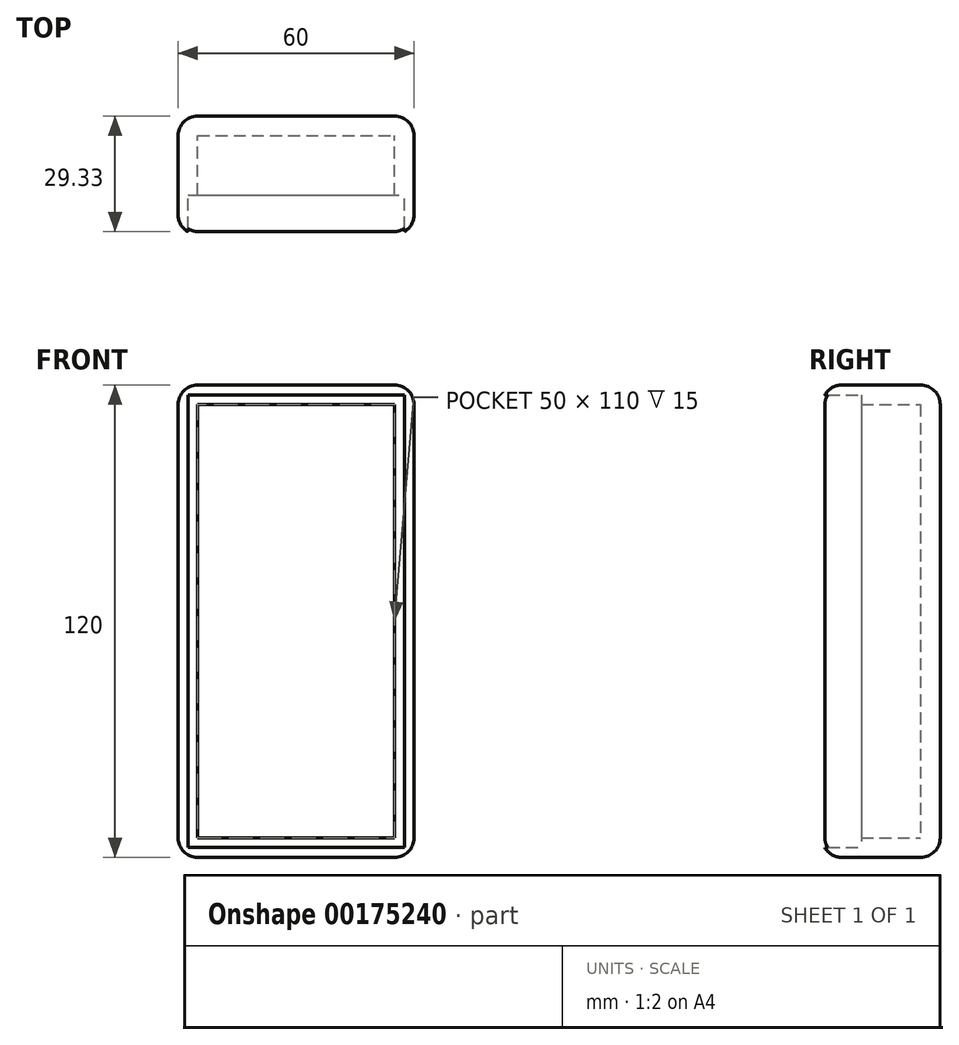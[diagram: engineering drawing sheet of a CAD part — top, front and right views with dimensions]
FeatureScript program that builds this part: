
annotation { "Feature Type Name" : "Feature", "Feature Type Description" : "" }
export const myFeature = defineFeature(function(context is Context, id is Id, definition is map)
    precondition{}
    {
        {
            var Q0;
            Q0=qCreatedBy(makeId("Front.planeOp"),FACE);
            var sketch = newSketch(context, id + "F0", { "sketchPlane" : qUnion([Q0])});
            skLineSegment(sketch, "E0.bottom", {"start": v(-21.77, 80.13) * mm, "end": v(33.23, 80.13) * mm});
            skLineSegment(sketch, "E0.top", {"start": v(-26.77, -39.87) * mm, "end": v(33.23, -39.87) * mm});
            skLineSegment(sketch, "E0.left", {"start": v(-26.77, 80.13) * mm, "end": v(-26.77, -39.87) * mm});
            skLineSegment(sketch, "E0.right", {"start": v(33.23, 80.13) * mm, "end": v(33.23, -39.87) * mm});
            skLineSegment(sketch, "E1.right", {"start": v(-21.77, 80.13) * mm, "end": v(-21.77, 80.13) * mm});
            skLineSegment(sketch, "E2.bottom", {"start": v(-21.77, 75.13) * mm, "end": v(28.23, 75.13) * mm});
            skLineSegment(sketch, "E2.top", {"start": v(-21.77, -34.87) * mm, "end": v(28.23, -34.87) * mm});
            skLineSegment(sketch, "E2.left", {"start": v(-21.77, 75.13) * mm, "end": v(-21.77, -34.87) * mm});
            skLineSegment(sketch, "E2.right", {"start": v(28.23, 75.13) * mm, "end": v(28.23, -34.87) * mm});
            skLineSegment(sketch, "E3", {"start": v(-21.77, 80.13) * mm, "end": v(-26.77, 80.13) * mm});
            skLineSegment(sketch, "E4", {"start": v(-26.77, 80.13) * mm, "end": v(-24.27, 80.13) * mm});
            skLineSegment(sketch, "E5.bottom", {"start": v(-24.27, 77.63) * mm, "end": v(30.73, 77.63) * mm});
            skLineSegment(sketch, "E5.top", {"start": v(-24.27, -37.37) * mm, "end": v(30.73, -37.37) * mm});
            skLineSegment(sketch, "E5.left", {"start": v(-24.27, 77.63) * mm, "end": v(-24.27, -37.37) * mm});
            skLineSegment(sketch, "E5.right", {"start": v(30.73, 77.63) * mm, "end": v(30.73, -37.37) * mm});
            skSolve(sketch);
        }
        {
            var Q0;
            Q0=makeQuery(id+"F0.imprint","IMPRINT",FACE,{"disambiguationData":[TD([[makeQuery(id+"F0.imprint","IMPRINT",EDGE,{"derivedFrom":sQuery(id+"F0.wireOp",EDGE,"E0.bottom")}),-1.0]])]});
            var Q1;
            Q1=makeQuery(id+"F0.imprint","IMPRINT",FACE,{"disambiguationData":[TD([[makeQuery(id+"F0.imprint","IMPRINT",EDGE,{"derivedFrom":sQuery(id+"F0.wireOp",EDGE,"E2.bottom")}),1.0]])]});
            extrude(context, id + "F1", {"entities" : qUnion([Q0, Q1]), "depth" : 20 * mm});
        }
        {
            var Q0;
            Q0=makeQuery(id+"F1.opExtrude","CAP_FACE",FACE,{"disambiguationData":[OSD([sQuery(id+"F0.wireOp",EDGE,"E0.bottom"),sQuery(id+"F0.wireOp",EDGE,"E0.top"),sQuery(id+"F0.wireOp",EDGE,"E0.left"),sQuery(id+"F0.wireOp",EDGE,"E0.right"),sQuery(id+"F0.wireOp",EDGE,"E2.bottom"),sQuery(id+"F0.wireOp",EDGE,"E2.top"),sQuery(id+"F0.wireOp",EDGE,"E2.left"),sQuery(id+"F0.wireOp",EDGE,"E2.right"),sQuery(id+"F0.wireOp",EDGE,"E3"),sQuery(id+"F0.wireOp",EDGE,"E4")])],"isStart":false});
            var sketch = newSketch(context, id + "F2", { "sketchPlane" : qUnion([Q0])});
            skLineSegment(sketch, "E6.left", {"start": v(-26.77, 80.13) * mm, "end": v(-26.77, 80.13) * mm});
            skLineSegment(sketch, "E6.right", {"start": v(-24.27, 80.13) * mm, "end": v(-24.27, 80.13) * mm});
            skLineSegment(sketch, "E7.bottom", {"start": v(-24.27, 77.63) * mm, "end": v(30.73, 77.63) * mm});
            skLineSegment(sketch, "E7.top", {"start": v(-24.27, -37.37) * mm, "end": v(30.73, -37.37) * mm});
            skLineSegment(sketch, "E7.left", {"start": v(-24.27, 77.63) * mm, "end": v(-24.27, -37.37) * mm});
            skLineSegment(sketch, "E7.right", {"start": v(30.73, 77.63) * mm, "end": v(30.73, -37.37) * mm});
            skPoint(sketch, "E8.end.orphan", {"position": v(-26.77, 77.63) * mm});
            skSolve(sketch);
        }
        {
            var Q0;
            Q0=makeQuery(id+"F2.imprint","IMPRINT",FACE,{"disambiguationData":[TD([[makeQuery(id+"F2.imprint","IMPRINT",EDGE,{"derivedFrom":sQuery(id+"F2.wireOp",EDGE,"E7.bottom")}),1.0]])]});
            extrude(context, id + "F3", {"entities" : qUnion([Q0]), "operationType" : NewBodyOperationType.ADD, "depth" : 10 * mm});
        }
        {
            var Q0;
            Q0=makeQuery(id+"F3.opExtrude","CAP_EDGE",EDGE,{"disambiguationData":[OSD([sQuery(id+"F0.wireOp",EDGE,"E0.top")])],"isStart":false});
            var Q1;
            Q1=makeQuery(id+"F3.opExtrude","CAP_EDGE",EDGE,{"disambiguationData":[OSD([sQuery(id+"F0.wireOp",EDGE,"E0.left")])],"isStart":false});
            var Q2;
            Q2=makeQuery(id+"F3.opExtrude","CAP_EDGE",EDGE,{"disambiguationData":[OSD([sQuery(id+"F0.wireOp",EDGE,"E0.bottom"),sQuery(id+"F0.wireOp",EDGE,"E3"),sQuery(id+"F0.wireOp",EDGE,"E4")])],"isStart":false});
            var Q3;
            Q3=makeQuery(id+"F3.opExtrude","CAP_EDGE",EDGE,{"disambiguationData":[OSD([sQuery(id+"F0.wireOp",EDGE,"E0.right")])],"isStart":false});
            fillet(context, id + "F4", {"entities" : qUnion([Q0, Q1, Q2, Q3]), "radius" : 5 * mm, "tangentPropagation" : true, "allowEdgeOverflow" : false});
        }
        {
            var Q0;
            Q0=makeQuery(id+"F1.opExtrude","CAP_FACE",FACE,{"disambiguationData":[OSD([sQuery(id+"F0.wireOp",EDGE,"E0.bottom"),sQuery(id+"F0.wireOp",EDGE,"E0.top"),sQuery(id+"F0.wireOp",EDGE,"E0.left"),sQuery(id+"F0.wireOp",EDGE,"E0.right"),sQuery(id+"F0.wireOp",EDGE,"E2.bottom"),sQuery(id+"F0.wireOp",EDGE,"E2.top"),sQuery(id+"F0.wireOp",EDGE,"E2.left"),sQuery(id+"F0.wireOp",EDGE,"E2.right"),sQuery(id+"F0.wireOp",EDGE,"E3"),sQuery(id+"F0.wireOp",EDGE,"E4")])],"isStart":true});
            var sketch = newSketch(context, id + "F5", { "sketchPlane" : qUnion([Q0])});
            skSolve(sketch);
        }
        {
            var Q0;
            Q0 = qSketchRegion(id + "F5", true);
            var Q1;
            Q1=makeQuery(id+"F5.imprint","IMPRINT",FACE,{"disambiguationData":[TD([[makeQuery(id+"F5.imprint","IMPRINT",EDGE,{"derivedFrom":makeQuery(id+"F1.opExtrude","CAP_EDGE",EDGE,{"disambiguationData":[OSD([sQuery(id+"F0.wireOp",EDGE,"E2.bottom")])],"isStart":true})}),1.0]])]});
            extrude(context, id + "F6", {"entities" : qUnion([Q0, Q1]), "operationType" : NewBodyOperationType.ADD, "oppositeDirection" : true, "depth" : 5 * mm});
        }
        {
            var Q0;
            {var subQ0=sQuery(id+"F0.wireOp",EDGE,"E0.right");var subQ1=sQuery(id+"F0.wireOp",EDGE,"E0.bottom");Q0=makeQuery(id+"F3.boolean.opBoolean","MERGE",EDGE,{"derivedFrom":[makeQuery(id+"F1.opExtrude","SWEPT_EDGE",EDGE,{"disambiguationData":[OSD([subQ1,subQ0])]}),makeQuery(id+"F3.opExtrude","SWEPT_EDGE",EDGE,{"disambiguationData":[OSD([subQ1,subQ0,sQuery(id+"F0.wireOp",EDGE,"E3"),sQuery(id+"F0.wireOp",EDGE,"E4")])]})]});}
            var Q1;
            Q1=makeQuery(id+"F1.opExtrude","CAP_EDGE",EDGE,{"disambiguationData":[OSD([sQuery(id+"F0.wireOp",EDGE,"E0.right")])],"isStart":true});
            var Q2;
            Q2=makeQuery(id+"F1.opExtrude","CAP_EDGE",EDGE,{"disambiguationData":[OSD([sQuery(id+"F0.wireOp",EDGE,"E0.bottom"),sQuery(id+"F0.wireOp",EDGE,"E3"),sQuery(id+"F0.wireOp",EDGE,"E4")])],"isStart":true});
            var Q3;
            Q3=makeQuery(id+"F1.opExtrude","CAP_EDGE",EDGE,{"disambiguationData":[OSD([sQuery(id+"F0.wireOp",EDGE,"E0.left")])],"isStart":true});
            var Q4;
            Q4=makeQuery(id+"F1.opExtrude","CAP_EDGE",EDGE,{"disambiguationData":[OSD([sQuery(id+"F0.wireOp",EDGE,"E0.top")])],"isStart":true});
            var Q5;
            {var subQ0=sQuery(id+"F0.wireOp",EDGE,"E0.right");var subQ1=sQuery(id+"F0.wireOp",EDGE,"E0.top");Q5=makeQuery(id+"F3.boolean.opBoolean","MERGE",EDGE,{"derivedFrom":[makeQuery(id+"F1.opExtrude","SWEPT_EDGE",EDGE,{"disambiguationData":[OSD([subQ1,subQ0])]}),makeQuery(id+"F3.opExtrude","SWEPT_EDGE",EDGE,{"disambiguationData":[OSD([subQ1,subQ0])]})]});}
            var Q6;
            {var subQ0=sQuery(id+"F0.wireOp",EDGE,"E0.left");var subQ1=sQuery(id+"F0.wireOp",EDGE,"E0.top");Q6=makeQuery(id+"F3.boolean.opBoolean","MERGE",EDGE,{"derivedFrom":[makeQuery(id+"F1.opExtrude","SWEPT_EDGE",EDGE,{"disambiguationData":[OSD([subQ1,subQ0])]}),makeQuery(id+"F3.opExtrude","SWEPT_EDGE",EDGE,{"disambiguationData":[OSD([subQ1,subQ0])]})]});}
            var Q7;
            {var subQ0=sQuery(id+"F0.wireOp",EDGE,"E4");var subQ1=sQuery(id+"F0.wireOp",EDGE,"E0.left");Q7=makeQuery(id+"F3.boolean.opBoolean","MERGE",EDGE,{"derivedFrom":[makeQuery(id+"F1.opExtrude","SWEPT_EDGE",EDGE,{"disambiguationData":[OSD([subQ1,subQ0])]}),makeQuery(id+"F3.opExtrude","SWEPT_EDGE",EDGE,{"disambiguationData":[OSD([sQuery(id+"F0.wireOp",EDGE,"E0.bottom"),subQ1,sQuery(id+"F0.wireOp",EDGE,"E3"),subQ0])]})]});}
            fillet(context, id + "F7", {"entities" : qUnion([Q0, Q1, Q2, Q3, Q4, Q5, Q6, Q7]), "radius" : 5 * mm, "tangentPropagation" : true, "allowEdgeOverflow" : false});
        }
    });
